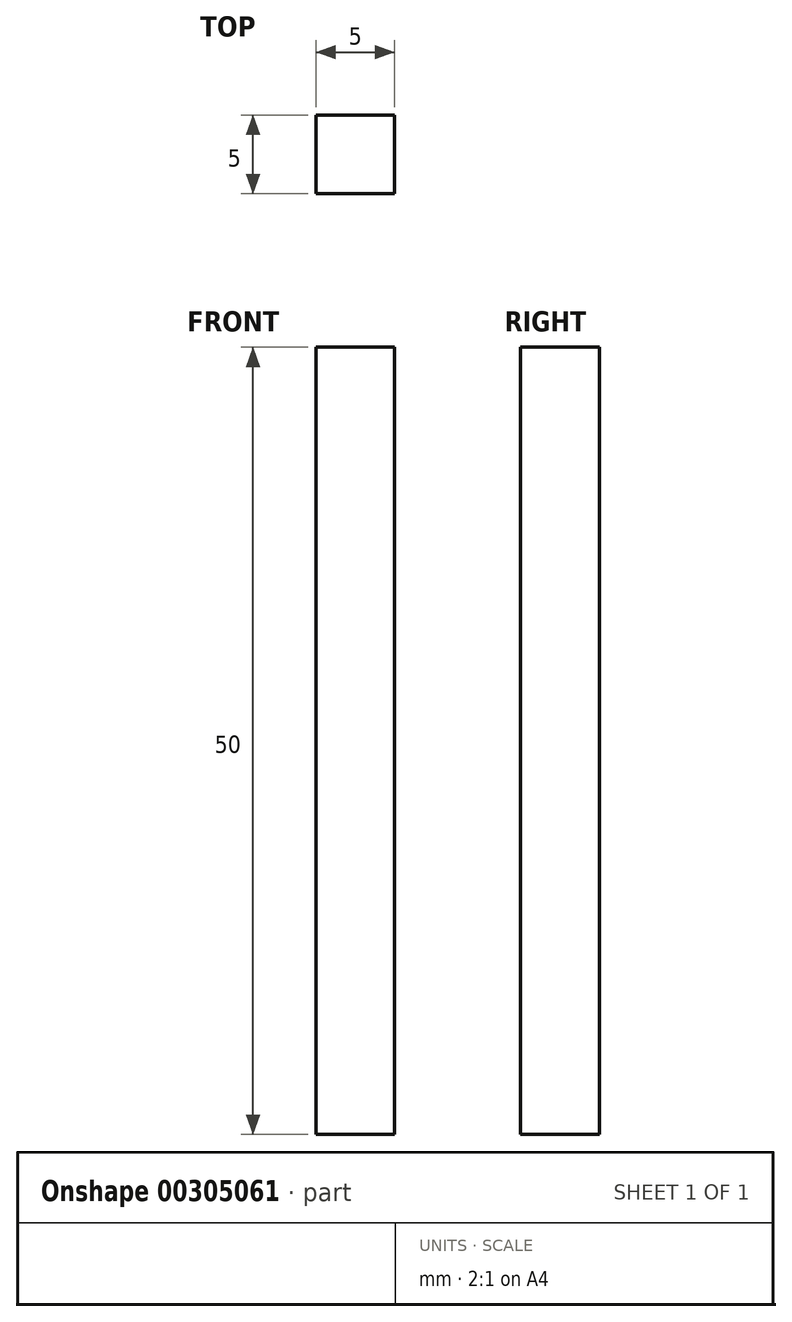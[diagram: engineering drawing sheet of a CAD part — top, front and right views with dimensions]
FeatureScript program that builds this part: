
annotation { "Feature Type Name" : "Feature", "Feature Type Description" : "" }
export const myFeature = defineFeature(function(context is Context, id is Id, definition is map)
    precondition{}
    {
        {
            var Q0;
            Q0=qCreatedBy(makeId("Top.planeOp"),FACE);
            var sketch = newSketch(context, id + "F0", { "sketchPlane" : qUnion([Q0])});
            skLineSegment(sketch, "E0.bottom", {"start": v(-2.5, -2.5) * mm, "end": v(2.5, -2.5) * mm});
            skLineSegment(sketch, "E0.top", {"start": v(-2.5, 2.5) * mm, "end": v(2.5, 2.5) * mm});
            skLineSegment(sketch, "E0.left", {"start": v(-2.5, -2.5) * mm, "end": v(-2.5, 2.5) * mm});
            skLineSegment(sketch, "E0.right", {"start": v(2.5, -2.5) * mm, "end": v(2.5, 2.5) * mm});
            skPoint(sketch, "E0.middle", {"position": v(0, 0) * mm});
            skSolve(sketch);
        }
        {
            var Q0;
            Q0 = qSketchRegion(id + "F0", true);
            extrude(context, id + "F1", {"entities" : qUnion([Q0]), "depth" : 50 * mm});
        }
    });
